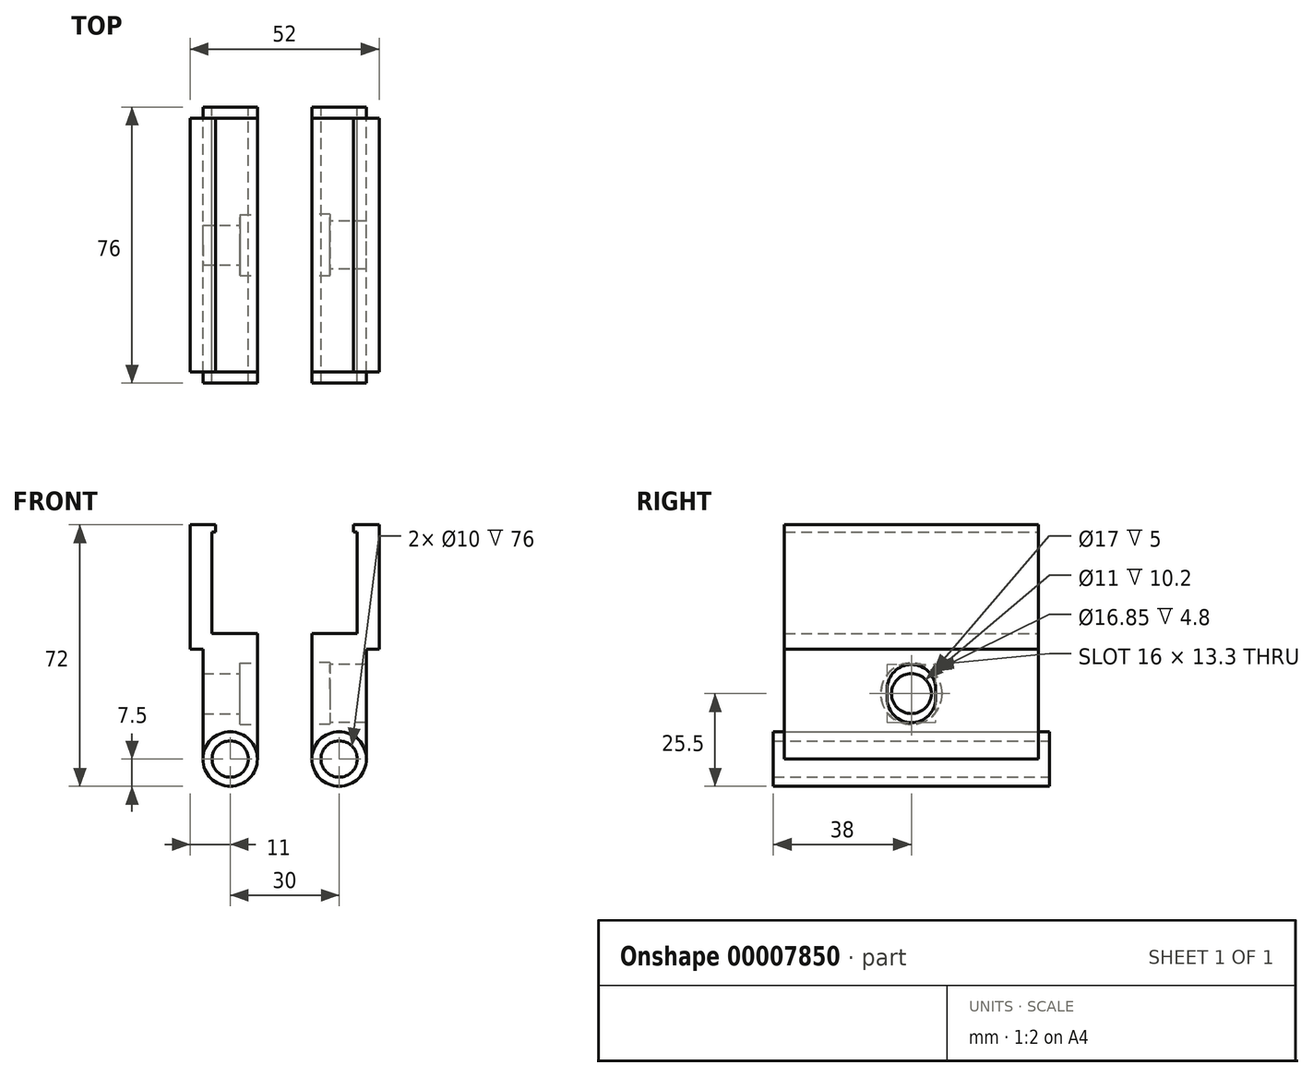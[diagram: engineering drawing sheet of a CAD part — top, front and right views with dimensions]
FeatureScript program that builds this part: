
annotation { "Feature Type Name" : "Feature", "Feature Type Description" : "" }
export const myFeature = defineFeature(function(context is Context, id is Id, definition is map)
    precondition{}
    {
        {
            var Q0;
            Q0=qCreatedBy(makeId("Front.planeOp"),FACE);
            var sketch = newSketch(context, id + "F0", { "sketchPlane" : qUnion([Q0])});
            skLineSegment(sketch, "E0", {"start": v(-26, 30) * mm, "end": v(-26, -4.3) * mm});
            skLineSegment(sketch, "E1", {"start": v(26, -4.3) * mm, "end": v(26, 30) * mm});
            skLineSegment(sketch, "E2", {"start": v(26, 30) * mm, "end": v(19, 30) * mm});
            skLineSegment(sketch, "E3", {"start": v(19, 30) * mm, "end": v(19, 28) * mm});
            skLineSegment(sketch, "E4", {"start": v(19, 28) * mm, "end": v(20, 28) * mm});
            skLineSegment(sketch, "E5", {"start": v(20, 28) * mm, "end": v(20, 0) * mm});
            skLineSegment(sketch, "E6", {"start": v(20, 0) * mm, "end": v(7.5, 0) * mm});
            skLineSegment(sketch, "E7", {"start": v(-20, 0) * mm, "end": v(-20, 28) * mm});
            skLineSegment(sketch, "E8", {"start": v(-20, 28) * mm, "end": v(-19, 28) * mm});
            skLineSegment(sketch, "E9", {"start": v(-19, 28) * mm, "end": v(-19, 30) * mm});
            skLineSegment(sketch, "E10", {"start": v(-19, 30) * mm, "end": v(-26, 30) * mm});
            skCircle(sketch, "E11", {"center": v(-15, -34.5) * mm, "radius": 5 * mm});
            skCircle(sketch, "E12", {"center": v(-15, -34.5) * mm, "radius": 7.5 * mm});
            skCircle(sketch, "E13", {"center": v(15, -34.5) * mm, "radius": 5 * mm});
            skCircle(sketch, "E14", {"center": v(15, -34.5) * mm, "radius": 7.5 * mm});
            skLineSegment(sketch, "E15", {"start": v(-15, -34.5) * mm, "end": v(15, -34.5) * mm, "construction": true});
            skLineSegment(sketch, "E16", {"start": v(-7.5, 0) * mm, "end": v(-7.5, -34.5) * mm});
            skLineSegment(sketch, "E17", {"start": v(7.5, 0) * mm, "end": v(7.5, -34.5) * mm});
            skLineSegment(sketch, "E18", {"start": v(22.5, -34.5) * mm, "end": v(22.5, -4.3) * mm});
            skLineSegment(sketch, "E19", {"start": v(22.5, -4.3) * mm, "end": v(26, -4.3) * mm});
            skLineSegment(sketch, "E20", {"start": v(-22.5, -34.5) * mm, "end": v(-22.5, -4.3) * mm});
            skLineSegment(sketch, "E21", {"start": v(-22.5, -4.3) * mm, "end": v(-26, -4.3) * mm});
            skLineSegment(sketch, "E22.trimOffspring", {"start": v(-7.5, 0) * mm, "end": v(-20, 0) * mm});
            skLineSegment(sketch, "E23", {"start": v(-20, 16.43) * mm, "end": v(20, 16.43) * mm, "construction": true});
            skLineSegment(sketch, "E24", {"start": v(14.94, -42) * mm, "end": v(-15, -42) * mm, "construction": true});
            skSolve(sketch);
        }
        {
            var Q0;
            Q0=makeQuery(id+"F0.imprint","IMPRINT",FACE,{"disambiguationData":[TD([[makeQuery(id+"F0.imprint","IMPRINT",EDGE,{"derivedFrom":sQuery(id+"F0.wireOp",EDGE,"E0")}),1.0]])]});
            var Q1;
            Q1=makeQuery(id+"F0.imprint","IMPRINT",FACE,{"disambiguationData":[TD([[makeQuery(id+"F0.imprint","IMPRINT",EDGE,{"derivedFrom":sQuery(id+"F0.wireOp",EDGE,"E1")}),1.0]])]});
            extrude(context, id + "F1", {"entities" : qUnion([Q0, Q1]), "endBound" : BoundingType.SYMMETRIC, "depth" : 76 * mm - 3.04 * mm * 2});
        }
        {
            var Q0;
            Q0=makeQuery(id+"F0.imprint","IMPRINT",FACE,{"disambiguationData":[TD([[makeQuery(id+"F0.imprint","IMPRINT",EDGE,{"derivedFrom":sQuery(id+"F0.wireOp",EDGE,"E11")}),-1.0]])]});
            var Q1;
            Q1=makeQuery(id+"F0.imprint","IMPRINT",FACE,{"disambiguationData":[TD([[makeQuery(id+"F0.imprint","IMPRINT",EDGE,{"derivedFrom":sQuery(id+"F0.wireOp",EDGE,"E13")}),-1.0]])]});
            extrude(context, id + "F2", {"entities" : qUnion([Q0, Q1]), "endBound" : BoundingType.SYMMETRIC, "depth" : 76 * mm});
        }
        {
            var Q0;
            Q0=makeQuery(id+"F1.opExtrude","SWEPT_FACE",FACE,{"disambiguationData":[OSD([sQuery(id+"F0.wireOp",EDGE,"E16")])]});
            var sketch = newSketch(context, id + "F3", { "sketchPlane" : qUnion([Q0])});
            skCircle(sketch, "E25", {"center": v(0, -16.5) * mm, "radius": 5.5 * mm});
            skLineSegment(sketch, "E26", {"start": v(0, -22) * mm, "end": v(0, -42) * mm, "construction": true});
            skCircle(sketch, "E27", {"center": v(0, -16.5) * mm, "radius": 8.43 * mm});
            skSolve(sketch);
        }
        {
            var Q0;
            Q0=makeQuery(id+"F3.imprint","IMPRINT",FACE,{"disambiguationData":[TD([[makeQuery(id+"F3.imprint","IMPRINT",EDGE,{"derivedFrom":sQuery(id+"F3.wireOp",EDGE,"E25")}),1.0]])]});
            extrude(context, id + "F4", {"entities" : qUnion([Q0]), "operationType" : NewBodyOperationType.REMOVE, "endBound" : BoundingType.UP_TO_NEXT, "oppositeDirection" : true, "depth" : 25.4 * mm});
        }
        {
            var Q0;
            Q0=makeQuery(id+"F3.imprint","IMPRINT",FACE,{"disambiguationData":[TD([[makeQuery(id+"F3.imprint","IMPRINT",EDGE,{"derivedFrom":sQuery(id+"F3.wireOp",EDGE,"E25")}),-1.0]])]});
            extrude(context, id + "F5", {"entities" : qUnion([Q0]), "operationType" : NewBodyOperationType.REMOVE, "oppositeDirection" : true, "depth" : 4.8 * mm});
        }
        {
            var Q0;
            Q0=makeQuery(id+"F1.opExtrude","SWEPT_FACE",FACE,{"disambiguationData":[OSD([sQuery(id+"F0.wireOp",EDGE,"E17")])]});
            var sketch = newSketch(context, id + "F6", { "sketchPlane" : qUnion([Q0])});
            skLineSegment(sketch, "E28", {"start": v(0, -8.5) * mm, "end": v(0, -24.5) * mm, "construction": true});
            skArc(sketch, "E29", {"start": v(6.65, -15.15) * mm, "mid": v(0, -8.5) * mm, "end": v(-6.65, -15.15) * mm});
            skArc(sketch, "E30", {"start": v(-6.65, -17.85) * mm, "mid": v(0, -24.5) * mm, "end": v(6.65, -17.85) * mm});
            skLineSegment(sketch, "E31", {"start": v(-6.65, -15.15) * mm, "end": v(-6.65, -17.85) * mm});
            skLineSegment(sketch, "E32", {"start": v(6.65, -15.15) * mm, "end": v(6.65, -17.85) * mm});
            skSolve(sketch);
        }
        {
            var Q0;
            Q0=makeQuery(id+"F6.imprint","IMPRINT",FACE,{"disambiguationData":[TD([[makeQuery(id+"F6.imprint","IMPRINT",EDGE,{"derivedFrom":sQuery(id+"F6.wireOp",EDGE,"E29")}),1.0]])]});
            extrude(context, id + "F7", {"entities" : qUnion([Q0]), "operationType" : NewBodyOperationType.REMOVE, "endBound" : BoundingType.UP_TO_NEXT, "oppositeDirection" : true, "depth" : 25.4 * mm});
        }
        {
            var Q0;
            Q0=makeQuery(id+"F1.opExtrude","SWEPT_FACE",FACE,{"disambiguationData":[OSD([sQuery(id+"F0.wireOp",EDGE,"E17")])]});
            var sketch = newSketch(context, id + "F8", { "sketchPlane" : qUnion([Q0])});
            skCircle(sketch, "E33", {"center": v(0, -16.5) * mm, "radius": 8.5 * mm});
            skSolve(sketch);
        }
        {
            var Q0;
            Q0=makeQuery(id+"F8.imprint","IMPRINT",FACE,{"disambiguationData":[TD([[makeQuery(id+"F8.imprint","IMPRINT",EDGE,{"derivedFrom":sQuery(id+"F8.wireOp",EDGE,"E33")}),1.0]])]});
            extrude(context, id + "F9", {"entities" : qUnion([Q0]), "operationType" : NewBodyOperationType.REMOVE, "oppositeDirection" : true, "depth" : 5 * mm});
        }
    });
